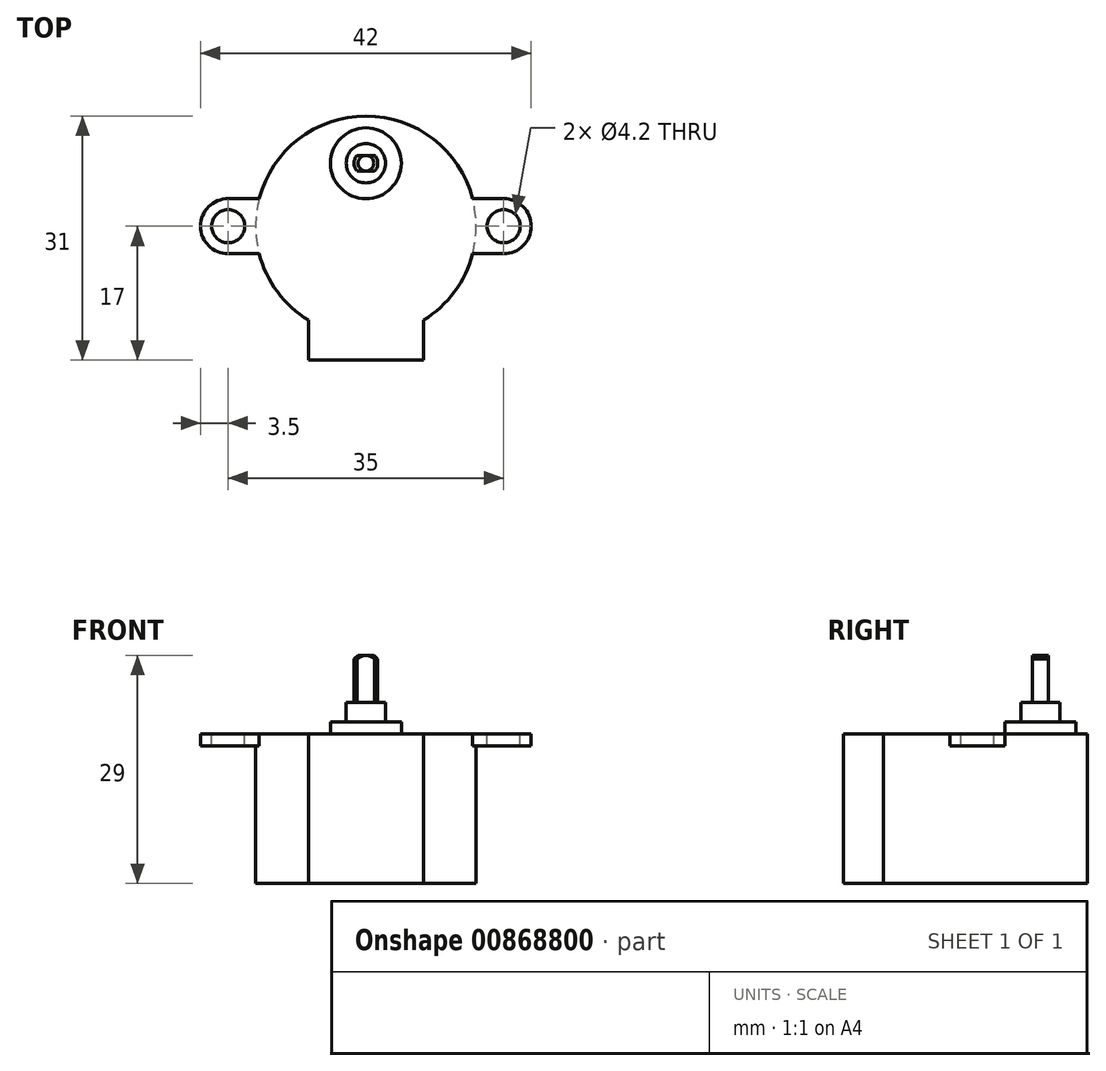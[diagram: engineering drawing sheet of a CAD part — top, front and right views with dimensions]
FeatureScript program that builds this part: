
annotation { "Feature Type Name" : "Feature", "Feature Type Description" : "" }
export const myFeature = defineFeature(function(context is Context, id is Id, definition is map)
    precondition{}
    {
        {
            var Q0;
            Q0=qCreatedBy(makeId("Top.planeOp"),FACE);
            var sketch = newSketch(context, id + "F0", { "sketchPlane" : qUnion([Q0])});
            skCircle(sketch, "E0", {"center": v(0, 0) * mm, "radius": 14 * mm});
            skLineSegment(sketch, "E1", {"start": v(0, 0) * mm, "end": v(-17.5, 0) * mm});
            skLineSegment(sketch, "E2", {"start": v(0, 0) * mm, "end": v(17.5, 0) * mm});
            skCircle(sketch, "E3", {"center": v(-17.5, 0) * mm, "radius": 2.1 * mm});
            skCircle(sketch, "E4", {"center": v(-17.5, 0) * mm, "radius": 3.5 * mm});
            skCircle(sketch, "E5", {"center": v(17.5, 0) * mm, "radius": 2.1 * mm});
            skCircle(sketch, "E6", {"center": v(17.5, 0) * mm, "radius": 3.5 * mm});
            skLineSegment(sketch, "E7.bottom", {"start": v(17.5, 3.5) * mm, "end": v(-17.5, 3.5) * mm});
            skLineSegment(sketch, "E7.top", {"start": v(17.5, -3.5) * mm, "end": v(-17.5, -3.5) * mm});
            skLineSegment(sketch, "E7.left", {"start": v(17.5, 3.5) * mm, "end": v(17.5, -3.5) * mm});
            skLineSegment(sketch, "E7.right", {"start": v(-17.5, 3.5) * mm, "end": v(-17.5, -3.5) * mm});
            skLineSegment(sketch, "E8.bottom", {"start": v(7.3, 17) * mm, "end": v(-7.3, 17) * mm});
            skLineSegment(sketch, "E8.top", {"start": v(7.3, -17) * mm, "end": v(-7.3, -17) * mm});
            skLineSegment(sketch, "E8.left", {"start": v(7.3, 17) * mm, "end": v(7.3, -17) * mm});
            skLineSegment(sketch, "E8.right", {"start": v(-7.3, 17) * mm, "end": v(-7.3, -17) * mm});
            skLineSegment(sketch, "E9", {"start": v(0, 0) * mm, "end": v(0, 8) * mm});
            skPoint(sketch, "E9.endSnap0", {"position": v(0, 3.5) * mm});
            skCircle(sketch, "E10", {"center": v(0, 8) * mm, "radius": 4.5 * mm});
            skCircle(sketch, "E11", {"center": v(0, 8) * mm, "radius": 2.5 * mm});
            skCircle(sketch, "E12", {"center": v(0, 8) * mm, "radius": 1.5 * mm});
            skSolve(sketch);
        }
        {
            var Q0;
            {var subQ0=sQuery(id+"F0.wireOp",EDGE,"E8.left");var subQ1=sQuery(id+"F0.wireOp",EDGE,"E0");var subQ2=makeQuery(id+"F0.imprint","INTERSECT",VERTEX,{"disambiguationData":[OD(1.0)],"derivedFrom":[subQ1,subQ0]});Q0=makeQuery(id+"F0.imprint","IMPRINT",FACE,{"disambiguationData":[TD([[makeQuery(id+"F0.imprint","IMPRINT",EDGE,{"disambiguationData":[TD([[subQ2,-1.0]])],"derivedFrom":subQ1}),1.0]])]});}
            var Q1;
            {var subQ0=sQuery(id+"F0.wireOp",EDGE,"E8.right");var subQ1=sQuery(id+"F0.wireOp",EDGE,"E0");var subQ2=makeQuery(id+"F0.imprint","INTERSECT",VERTEX,{"disambiguationData":[OD(1.0)],"derivedFrom":[subQ1,subQ0]});Q1=makeQuery(id+"F0.imprint","IMPRINT",FACE,{"disambiguationData":[TD([[makeQuery(id+"F0.imprint","IMPRINT",EDGE,{"disambiguationData":[TD([[subQ2,-1.0]])],"derivedFrom":subQ1}),1.0]])]});}
            var Q2;
            {var subQ0=sQuery(id+"F0.wireOp",EDGE,"E7.top");var subQ1=sQuery(id+"F0.wireOp",EDGE,"E0");var subQ2=makeQuery(id+"F0.imprint","INTERSECT",VERTEX,{"disambiguationData":[OD(0.0)],"derivedFrom":[subQ1,subQ0]});Q2=makeQuery(id+"F0.imprint","IMPRINT",FACE,{"disambiguationData":[TD([[makeQuery(id+"F0.imprint","IMPRINT",EDGE,{"disambiguationData":[TD([[subQ2,-1.0]])],"derivedFrom":subQ1}),1.0]])]});}
            var Q3;
            {var subQ0=sQuery(id+"F0.wireOp",EDGE,"E7.top");var subQ1=sQuery(id+"F0.wireOp",EDGE,"E0");var subQ2=makeQuery(id+"F0.imprint","INTERSECT",VERTEX,{"disambiguationData":[OD(0.0)],"derivedFrom":[subQ1,subQ0]});Q3=makeQuery(id+"F0.imprint","IMPRINT",FACE,{"disambiguationData":[TD([[makeQuery(id+"F0.imprint","IMPRINT",EDGE,{"disambiguationData":[TD([[subQ2,1.0]])],"derivedFrom":subQ0}),-1.0]])]});}
            var Q4;
            {var subQ0=sQuery(id+"F0.wireOp",EDGE,"E7.bottom");var subQ1=sQuery(id+"F0.wireOp",EDGE,"E0");var subQ2=makeQuery(id+"F0.imprint","INTERSECT",VERTEX,{"disambiguationData":[OD(1.0)],"derivedFrom":[subQ1,subQ0]});Q4=makeQuery(id+"F0.imprint","IMPRINT",FACE,{"disambiguationData":[TD([[makeQuery(id+"F0.imprint","IMPRINT",EDGE,{"disambiguationData":[TD([[subQ2,1.0]])],"derivedFrom":subQ0}),1.0]])]});}
            var Q5;
            {var subQ0=sQuery(id+"F0.wireOp",EDGE,"E8.right");var subQ1=sQuery(id+"F0.wireOp",EDGE,"E0");var subQ2=makeQuery(id+"F0.imprint","INTERSECT",VERTEX,{"disambiguationData":[OD(0.0)],"derivedFrom":[subQ1,subQ0]});Q5=makeQuery(id+"F0.imprint","IMPRINT",FACE,{"disambiguationData":[TD([[makeQuery(id+"F0.imprint","IMPRINT",EDGE,{"disambiguationData":[TD([[subQ2,-1.0]])],"derivedFrom":subQ1}),1.0]])]});}
            var Q6;
            {var subQ0=sQuery(id+"F0.wireOp",EDGE,"E10");Q6=makeQuery(id+"F0.imprint","IMPRINT",FACE,{"disambiguationData":[TD([[makeQuery(id+"F0.imprint","IMPRINT",EDGE,{"derivedFrom":subQ0}),-1.0]])]});}
            var Q7;
            {var subQ0=sQuery(id+"F0.wireOp",EDGE,"E7.bottom");var subQ1=sQuery(id+"F0.wireOp",EDGE,"E0");var subQ2=makeQuery(id+"F0.imprint","INTERSECT",VERTEX,{"disambiguationData":[OD(0.0)],"derivedFrom":[subQ1,subQ0]});Q7=makeQuery(id+"F0.imprint","IMPRINT",FACE,{"disambiguationData":[TD([[makeQuery(id+"F0.imprint","IMPRINT",EDGE,{"disambiguationData":[TD([[subQ2,-1.0]])],"derivedFrom":subQ1}),1.0]])]});}
            var Q8;
            {var subQ0=sQuery(id+"F0.wireOp",EDGE,"E7.bottom");var subQ1=sQuery(id+"F0.wireOp",EDGE,"E0");var subQ2=makeQuery(id+"F0.imprint","INTERSECT",VERTEX,{"disambiguationData":[OD(0.0)],"derivedFrom":[subQ1,subQ0]});Q8=makeQuery(id+"F0.imprint","IMPRINT",FACE,{"disambiguationData":[TD([[makeQuery(id+"F0.imprint","IMPRINT",EDGE,{"disambiguationData":[TD([[subQ2,-1.0]])],"derivedFrom":subQ0}),1.0]])]});}
            var Q9;
            {var subQ0=sQuery(id+"F0.wireOp",EDGE,"E7.top");var subQ1=sQuery(id+"F0.wireOp",EDGE,"E0");var subQ2=makeQuery(id+"F0.imprint","INTERSECT",VERTEX,{"disambiguationData":[OD(1.0)],"derivedFrom":[subQ1,subQ0]});Q9=makeQuery(id+"F0.imprint","IMPRINT",FACE,{"disambiguationData":[TD([[makeQuery(id+"F0.imprint","IMPRINT",EDGE,{"disambiguationData":[TD([[subQ2,-1.0]])],"derivedFrom":subQ0}),-1.0]])]});}
            var Q10;
            {var subQ0=sQuery(id+"F0.wireOp",EDGE,"E8.left");var subQ1=sQuery(id+"F0.wireOp",EDGE,"E7.top");var subQ2=makeQuery(id+"F0.imprint","INTERSECT",VERTEX,{"derivedFrom":[subQ1,subQ0]});Q10=makeQuery(id+"F0.imprint","IMPRINT",FACE,{"disambiguationData":[TD([[makeQuery(id+"F0.imprint","IMPRINT",EDGE,{"disambiguationData":[TD([[subQ2,-1.0]])],"derivedFrom":subQ1}),-1.0]])]});}
            var Q11;
            {var subQ1=sQuery(id+"F0.wireOp",EDGE,"E2");var subQ3=sQuery(id+"F0.wireOp",EDGE,"E8.left");var subQ4=makeQuery(id+"F0.imprint","INTERSECT",VERTEX,{"derivedFrom":[subQ1,subQ3]});Q11=makeQuery(id+"F0.imprint","IMPRINT",FACE,{"disambiguationData":[TD([[makeQuery(id+"F0.imprint","IMPRINT",EDGE,{"disambiguationData":[TD([[subQ4,1.0]])],"derivedFrom":subQ3}),-1.0]])]});}
            var Q12;
            {var subQ1=sQuery(id+"F0.wireOp",EDGE,"E1");var subQ3=sQuery(id+"F0.wireOp",EDGE,"E8.right");var subQ4=makeQuery(id+"F0.imprint","INTERSECT",VERTEX,{"derivedFrom":[subQ1,subQ3]});Q12=makeQuery(id+"F0.imprint","IMPRINT",FACE,{"disambiguationData":[TD([[makeQuery(id+"F0.imprint","IMPRINT",EDGE,{"disambiguationData":[TD([[subQ4,1.0]])],"derivedFrom":subQ3}),1.0]])]});}
            var Q13;
            Q13=makeQuery(id+"F0.imprint","IMPRINT",FACE,{"disambiguationData":[TD([[makeQuery(id+"F0.imprint","IMPRINT",EDGE,{"derivedFrom":sQuery(id+"F0.wireOp",EDGE,"E10")}),1.0]])]});
            var Q14;
            Q14=makeQuery(id+"F0.imprint","IMPRINT",FACE,{"disambiguationData":[TD([[makeQuery(id+"F0.imprint","IMPRINT",EDGE,{"derivedFrom":sQuery(id+"F0.wireOp",EDGE,"E11")}),1.0]])]});
            var Q15;
            Q15=makeQuery(id+"F0.imprint","IMPRINT",FACE,{"disambiguationData":[TD([[makeQuery(id+"F0.imprint","IMPRINT",EDGE,{"derivedFrom":sQuery(id+"F0.wireOp",EDGE,"E12")}),1.0]])]});
            var Q16;
            {var subQ5=sQuery(id+"F0.wireOp",EDGE,"E8.top");Q16=makeQuery(id+"F0.imprint","IMPRINT",FACE,{"disambiguationData":[TD([[makeQuery(id+"F0.imprint","IMPRINT",EDGE,{"derivedFrom":subQ5}),-1.0]])]});}
            extrude(context, id + "F1", {"entities" : qUnion([Q0, Q1, Q2, Q3, Q4, Q5, Q6, Q7, Q8, Q9, Q10, Q11, Q12, Q13, Q14, Q15, Q16]), "oppositeDirection" : true, "depth" : 19 * mm, "offsetDistance" : 25 * mm});
        }
        {
            var Q0;
            {var subQ0=sQuery(id+"F0.wireOp",EDGE,"E7.right");var subQ1=sQuery(id+"F0.wireOp",EDGE,"E3");var subQ2=makeQuery(id+"F0.imprint","INTERSECT",VERTEX,{"disambiguationData":[OD(0.0)],"derivedFrom":[subQ1,subQ0]});Q0=makeQuery(id+"F0.imprint","IMPRINT",FACE,{"disambiguationData":[TD([[makeQuery(id+"F0.imprint","IMPRINT",EDGE,{"disambiguationData":[TD([[subQ2,-1.0]])],"derivedFrom":subQ1}),-1.0]])]});}
            var Q1;
            {var subQ0=sQuery(id+"F0.wireOp",EDGE,"E3");var subQ1=sQuery(id+"F0.wireOp",EDGE,"E1");var subQ2=makeQuery(id+"F0.imprint","INTERSECT",VERTEX,{"derivedFrom":[subQ1,subQ0]});Q1=makeQuery(id+"F0.imprint","IMPRINT",FACE,{"disambiguationData":[TD([[makeQuery(id+"F0.imprint","IMPRINT",EDGE,{"disambiguationData":[TD([[subQ2,1.0]])],"derivedFrom":subQ0}),-1.0]])]});}
            var Q2;
            {var subQ0=sQuery(id+"F0.wireOp",EDGE,"E7.top");var subQ1=sQuery(id+"F0.wireOp",EDGE,"E0");var subQ2=makeQuery(id+"F0.imprint","INTERSECT",VERTEX,{"disambiguationData":[OD(0.0)],"derivedFrom":[subQ1,subQ0]});Q2=makeQuery(id+"F0.imprint","IMPRINT",FACE,{"disambiguationData":[TD([[makeQuery(id+"F0.imprint","IMPRINT",EDGE,{"disambiguationData":[TD([[subQ2,1.0]])],"derivedFrom":subQ1}),-1.0]])]});}
            var Q3;
            {var subQ0=sQuery(id+"F0.wireOp",EDGE,"E3");var subQ1=sQuery(id+"F0.wireOp",EDGE,"E1");var subQ2=makeQuery(id+"F0.imprint","INTERSECT",VERTEX,{"derivedFrom":[subQ1,subQ0]});Q3=makeQuery(id+"F0.imprint","IMPRINT",FACE,{"disambiguationData":[TD([[makeQuery(id+"F0.imprint","IMPRINT",EDGE,{"disambiguationData":[TD([[subQ2,-1.0]])],"derivedFrom":subQ0}),-1.0]])]});}
            var Q4;
            {var subQ0=sQuery(id+"F0.wireOp",EDGE,"E7.bottom");var subQ1=sQuery(id+"F0.wireOp",EDGE,"E0");var subQ2=makeQuery(id+"F0.imprint","INTERSECT",VERTEX,{"disambiguationData":[OD(1.0)],"derivedFrom":[subQ1,subQ0]});Q4=makeQuery(id+"F0.imprint","IMPRINT",FACE,{"disambiguationData":[TD([[makeQuery(id+"F0.imprint","IMPRINT",EDGE,{"disambiguationData":[TD([[subQ2,-1.0]])],"derivedFrom":subQ1}),-1.0]])]});}
            var Q5;
            {var subQ0=sQuery(id+"F0.wireOp",EDGE,"E7.bottom");var subQ1=sQuery(id+"F0.wireOp",EDGE,"E0");var subQ2=makeQuery(id+"F0.imprint","INTERSECT",VERTEX,{"disambiguationData":[OD(0.0)],"derivedFrom":[subQ1,subQ0]});Q5=makeQuery(id+"F0.imprint","IMPRINT",FACE,{"disambiguationData":[TD([[makeQuery(id+"F0.imprint","IMPRINT",EDGE,{"disambiguationData":[TD([[subQ2,1.0]])],"derivedFrom":subQ1}),-1.0]])]});}
            var Q6;
            {var subQ0=sQuery(id+"F0.wireOp",EDGE,"E7.top");var subQ1=sQuery(id+"F0.wireOp",EDGE,"E0");var subQ2=makeQuery(id+"F0.imprint","INTERSECT",VERTEX,{"disambiguationData":[OD(1.0)],"derivedFrom":[subQ1,subQ0]});Q6=makeQuery(id+"F0.imprint","IMPRINT",FACE,{"disambiguationData":[TD([[makeQuery(id+"F0.imprint","IMPRINT",EDGE,{"disambiguationData":[TD([[subQ2,-1.0]])],"derivedFrom":subQ1}),-1.0]])]});}
            var Q7;
            {var subQ0=sQuery(id+"F0.wireOp",EDGE,"E7.left");var subQ1=sQuery(id+"F0.wireOp",EDGE,"E5");var subQ2=makeQuery(id+"F0.imprint","INTERSECT",VERTEX,{"disambiguationData":[OD(0.0)],"derivedFrom":[subQ1,subQ0]});Q7=makeQuery(id+"F0.imprint","IMPRINT",FACE,{"disambiguationData":[TD([[makeQuery(id+"F0.imprint","IMPRINT",EDGE,{"disambiguationData":[TD([[subQ2,1.0]])],"derivedFrom":subQ1}),-1.0]])]});}
            var Q8;
            {var subQ0=sQuery(id+"F0.wireOp",EDGE,"E5");var subQ1=sQuery(id+"F0.wireOp",EDGE,"E2");var subQ2=makeQuery(id+"F0.imprint","INTERSECT",VERTEX,{"derivedFrom":[subQ1,subQ0]});Q8=makeQuery(id+"F0.imprint","IMPRINT",FACE,{"disambiguationData":[TD([[makeQuery(id+"F0.imprint","IMPRINT",EDGE,{"disambiguationData":[TD([[subQ2,-1.0]])],"derivedFrom":subQ0}),-1.0]])]});}
            var Q9;
            {var subQ0=sQuery(id+"F0.wireOp",EDGE,"E5");var subQ1=sQuery(id+"F0.wireOp",EDGE,"E2");var subQ2=makeQuery(id+"F0.imprint","INTERSECT",VERTEX,{"derivedFrom":[subQ1,subQ0]});Q9=makeQuery(id+"F0.imprint","IMPRINT",FACE,{"disambiguationData":[TD([[makeQuery(id+"F0.imprint","IMPRINT",EDGE,{"disambiguationData":[TD([[subQ2,1.0]])],"derivedFrom":subQ0}),-1.0]])]});}
            extrude(context, id + "F2", {"entities" : qUnion([Q0, Q1, Q2, Q3, Q4, Q5, Q6, Q7, Q8, Q9]), "operationType" : NewBodyOperationType.ADD, "oppositeDirection" : true, "depth" : 1.5 * mm, "offsetDistance" : 25 * mm});
        }
        {
            var Q0;
            Q0=makeQuery(id+"F0.imprint","IMPRINT",FACE,{"disambiguationData":[TD([[makeQuery(id+"F0.imprint","IMPRINT",EDGE,{"derivedFrom":sQuery(id+"F0.wireOp",EDGE,"E12")}),1.0]])]});
            extrude(context, id + "F3", {"entities" : qUnion([Q0]), "operationType" : NewBodyOperationType.ADD, "depth" : 10 * mm, "offsetDistance" : 25 * mm});
        }
        {
            var Q0;
            Q0=makeQuery(id+"F0.imprint","IMPRINT",FACE,{"disambiguationData":[TD([[makeQuery(id+"F0.imprint","IMPRINT",EDGE,{"derivedFrom":sQuery(id+"F0.wireOp",EDGE,"E11")}),1.0]])]});
            extrude(context, id + "F4", {"entities" : qUnion([Q0]), "operationType" : NewBodyOperationType.ADD, "depth" : 4 * mm, "offsetDistance" : 25 * mm});
        }
        {
            var Q0;
            Q0=makeQuery(id+"F0.imprint","IMPRINT",FACE,{"disambiguationData":[TD([[makeQuery(id+"F0.imprint","IMPRINT",EDGE,{"derivedFrom":sQuery(id+"F0.wireOp",EDGE,"E10")}),1.0]])]});
            extrude(context, id + "F5", {"entities" : qUnion([Q0]), "operationType" : NewBodyOperationType.ADD, "depth" : 1.5 * mm, "offsetDistance" : 25 * mm});
        }
        {
            var Q0;
            Q0=makeQuery(id+"F3.opExtrude","CAP_EDGE",EDGE,{"disambiguationData":[OSD([sQuery(id+"F0.wireOp",EDGE,"E12")])],"isStart":false});
            chamfer(context, id + "F6", {"entities" : qUnion([Q0]), "width" : 0.5 * mm, "tangentPropagation" : true});
        }
        {
            var Q0;
            Q0=makeQuery(id+"F3.opExtrude","CAP_FACE",FACE,{"disambiguationData":[OSD([sQuery(id+"F0.wireOp",EDGE,"E12")])],"isStart":false});
            var sketch = newSketch(context, id + "F7", { "sketchPlane" : qUnion([Q0])});
            skLineSegment(sketch, "E13.bottom", {"start": v(1.5, 7) * mm, "end": v(-1.5, 7) * mm});
            skLineSegment(sketch, "E13.top", {"start": v(1.5, 9) * mm, "end": v(-1.5, 9) * mm});
            skLineSegment(sketch, "E13.left", {"start": v(1.5, 7) * mm, "end": v(1.5, 9) * mm});
            skLineSegment(sketch, "E13.right", {"start": v(-1.5, 7) * mm, "end": v(-1.5, 9) * mm});
            skPoint(sketch, "E13.middle", {"position": v(0, 8) * mm});
            skLineSegment(sketch, "E14.bottom", {"start": v(1.5, 6.5) * mm, "end": v(-1.5, 6.5) * mm});
            skLineSegment(sketch, "E14.top", {"start": v(1.5, 9.5) * mm, "end": v(-1.5, 9.5) * mm});
            skLineSegment(sketch, "E14.left", {"start": v(1.5, 6.5) * mm, "end": v(1.5, 9.5) * mm});
            skLineSegment(sketch, "E14.right", {"start": v(-1.5, 6.5) * mm, "end": v(-1.5, 9.5) * mm});
            skSolve(sketch);
        }
        {
            var Q0;
            {var subQ0=sQuery(id+"F7.wireOp",EDGE,"E14.top");Q0=makeQuery(id+"F7.imprint","IMPRINT",FACE,{"disambiguationData":[TD([[makeQuery(id+"F7.imprint","IMPRINT",EDGE,{"derivedFrom":subQ0}),1.0]])]});}
            var Q1;
            {var subQ0=sQuery(id+"F7.wireOp",EDGE,"E14.bottom");Q1=makeQuery(id+"F7.imprint","IMPRINT",FACE,{"disambiguationData":[TD([[makeQuery(id+"F7.imprint","IMPRINT",EDGE,{"derivedFrom":subQ0}),-1.0]])]});}
            extrude(context, id + "F8", {"entities" : qUnion([Q0, Q1]), "operationType" : NewBodyOperationType.REMOVE, "oppositeDirection" : true, "depth" : 6 * mm, "offsetDistance" : 25 * mm});
        }
    });
